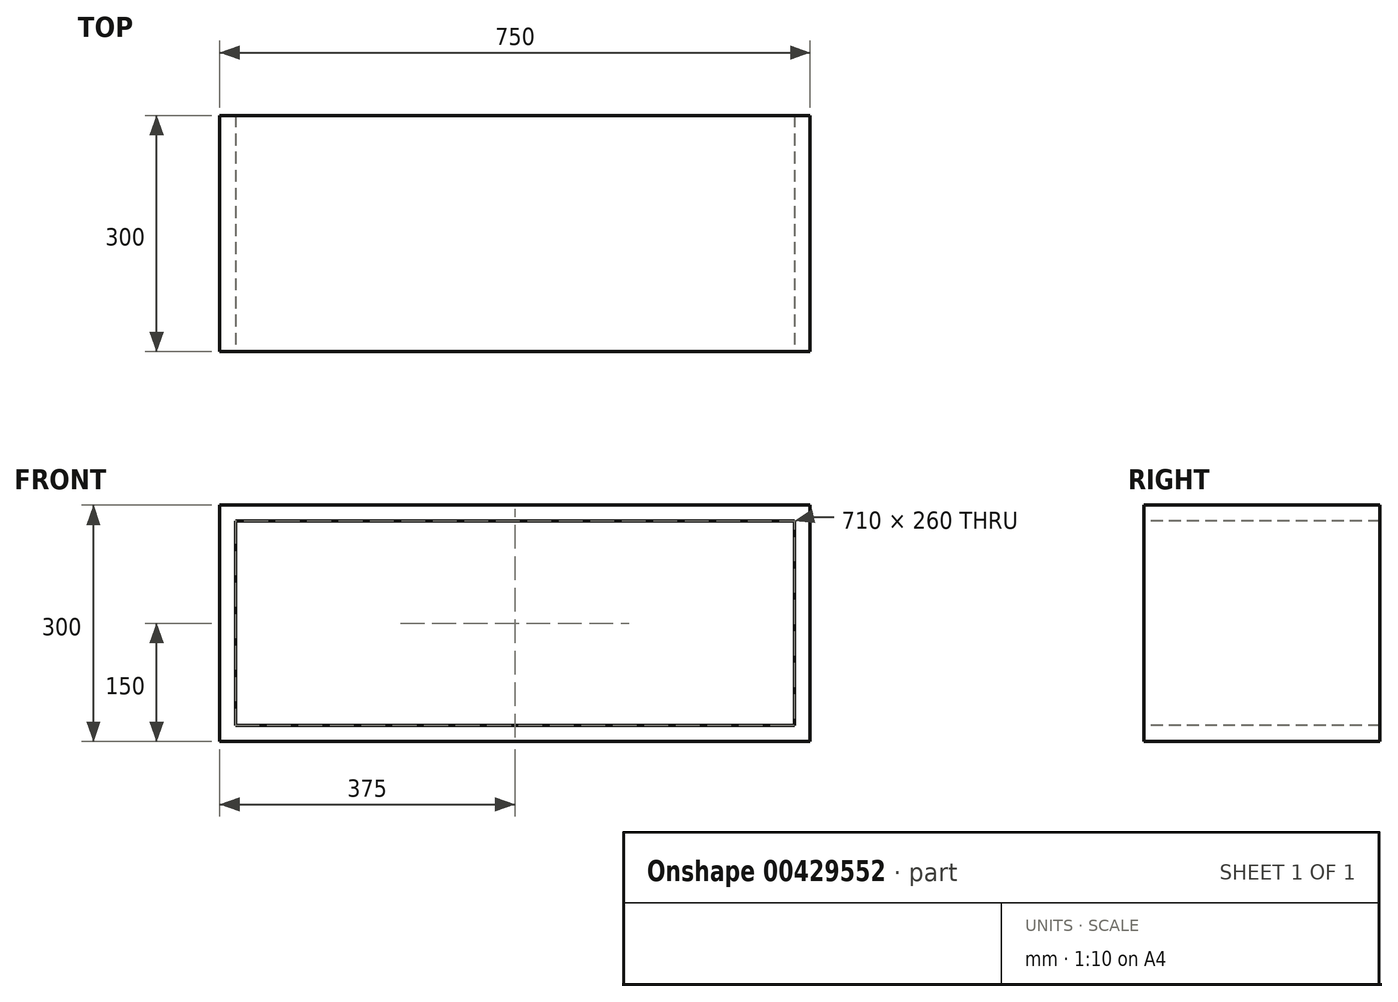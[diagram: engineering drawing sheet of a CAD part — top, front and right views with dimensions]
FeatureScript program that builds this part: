
annotation { "Feature Type Name" : "Feature", "Feature Type Description" : "" }
export const myFeature = defineFeature(function(context is Context, id is Id, definition is map)
    precondition{}
    {
        {
            var Q0;
            Q0=qCreatedBy(makeId("Front.planeOp"),FACE);
            var sketch = newSketch(context, id + "F0", { "sketchPlane" : qUnion([Q0])});
            skLineSegment(sketch, "E0.bottom", {"start": v(375, -150) * mm, "end": v(-375, -150) * mm});
            skLineSegment(sketch, "E0.top", {"start": v(375, 150) * mm, "end": v(-375, 150) * mm});
            skLineSegment(sketch, "E0.left", {"start": v(375, -150) * mm, "end": v(375, 150) * mm});
            skLineSegment(sketch, "E0.right", {"start": v(-375, -150) * mm, "end": v(-375, 150) * mm});
            skPoint(sketch, "E0.middle", {"position": v(0, 0) * mm});
            skLineSegment(sketch, "E1.0", {"start": v(355, -150) * mm, "end": v(355, 150) * mm});
            skLineSegment(sketch, "E2.0", {"start": v(375, 130) * mm, "end": v(-375, 130) * mm});
            skLineSegment(sketch, "E3.0", {"start": v(-355, -150) * mm, "end": v(-355, 150) * mm});
            skLineSegment(sketch, "E4.0", {"start": v(375, -130) * mm, "end": v(-375, -130) * mm});
            skSolve(sketch);
        }
        {
            var Q0;
            {var subQ0=sQuery(id+"F0.wireOp",EDGE,"E1.0");var subQ1=sQuery(id+"F0.wireOp",EDGE,"E0.top");var subQ2=makeQuery(id+"F0.imprint","INTERSECT",VERTEX,{"derivedFrom":[subQ1,subQ0]});Q0=makeQuery(id+"F0.imprint","IMPRINT",FACE,{"disambiguationData":[TD([[makeQuery(id+"F0.imprint","IMPRINT",EDGE,{"disambiguationData":[TD([[subQ2,-1.0]])],"derivedFrom":subQ1}),1.0]])]});}
            var Q1;
            {var subQ0=sQuery(id+"F0.wireOp",EDGE,"E0.right");var subQ1=sQuery(id+"F0.wireOp",EDGE,"E0.top");var subQ2=makeQuery(id+"F0.imprint","INTERSECT",VERTEX,{"derivedFrom":[subQ1,subQ0]});Q1=makeQuery(id+"F0.imprint","IMPRINT",FACE,{"disambiguationData":[TD([[makeQuery(id+"F0.imprint","IMPRINT",EDGE,{"disambiguationData":[TD([[subQ2,1.0]])],"derivedFrom":subQ1}),1.0]])]});}
            var Q2;
            {var subQ0=sQuery(id+"F0.wireOp",EDGE,"E2.0");var subQ1=sQuery(id+"F0.wireOp",EDGE,"E0.right");var subQ2=makeQuery(id+"F0.imprint","INTERSECT",VERTEX,{"derivedFrom":[subQ1,subQ0]});Q2=makeQuery(id+"F0.imprint","IMPRINT",FACE,{"disambiguationData":[TD([[makeQuery(id+"F0.imprint","IMPRINT",EDGE,{"disambiguationData":[TD([[subQ2,1.0]])],"derivedFrom":subQ1}),-1.0]])]});}
            var Q3;
            {var subQ0=sQuery(id+"F0.wireOp",EDGE,"E0.right");var subQ1=sQuery(id+"F0.wireOp",EDGE,"E0.bottom");var subQ2=makeQuery(id+"F0.imprint","INTERSECT",VERTEX,{"derivedFrom":[subQ1,subQ0]});Q3=makeQuery(id+"F0.imprint","IMPRINT",FACE,{"disambiguationData":[TD([[makeQuery(id+"F0.imprint","IMPRINT",EDGE,{"disambiguationData":[TD([[subQ2,1.0]])],"derivedFrom":subQ1}),-1.0]])]});}
            var Q4;
            {var subQ0=sQuery(id+"F0.wireOp",EDGE,"E1.0");var subQ1=sQuery(id+"F0.wireOp",EDGE,"E0.bottom");var subQ2=makeQuery(id+"F0.imprint","INTERSECT",VERTEX,{"derivedFrom":[subQ1,subQ0]});Q4=makeQuery(id+"F0.imprint","IMPRINT",FACE,{"disambiguationData":[TD([[makeQuery(id+"F0.imprint","IMPRINT",EDGE,{"disambiguationData":[TD([[subQ2,-1.0]])],"derivedFrom":subQ1}),-1.0]])]});}
            var Q5;
            {var subQ0=sQuery(id+"F0.wireOp",EDGE,"E0.left");var subQ1=sQuery(id+"F0.wireOp",EDGE,"E0.bottom");var subQ2=makeQuery(id+"F0.imprint","INTERSECT",VERTEX,{"derivedFrom":[subQ1,subQ0]});Q5=makeQuery(id+"F0.imprint","IMPRINT",FACE,{"disambiguationData":[TD([[makeQuery(id+"F0.imprint","IMPRINT",EDGE,{"disambiguationData":[TD([[subQ2,-1.0]])],"derivedFrom":subQ1}),-1.0]])]});}
            var Q6;
            {var subQ0=sQuery(id+"F0.wireOp",EDGE,"E2.0");var subQ1=sQuery(id+"F0.wireOp",EDGE,"E0.left");var subQ2=makeQuery(id+"F0.imprint","INTERSECT",VERTEX,{"derivedFrom":[subQ1,subQ0]});Q6=makeQuery(id+"F0.imprint","IMPRINT",FACE,{"disambiguationData":[TD([[makeQuery(id+"F0.imprint","IMPRINT",EDGE,{"disambiguationData":[TD([[subQ2,1.0]])],"derivedFrom":subQ1}),1.0]])]});}
            var Q7;
            {var subQ0=sQuery(id+"F0.wireOp",EDGE,"E0.left");var subQ1=sQuery(id+"F0.wireOp",EDGE,"E0.top");var subQ2=makeQuery(id+"F0.imprint","INTERSECT",VERTEX,{"derivedFrom":[subQ1,subQ0]});Q7=makeQuery(id+"F0.imprint","IMPRINT",FACE,{"disambiguationData":[TD([[makeQuery(id+"F0.imprint","IMPRINT",EDGE,{"disambiguationData":[TD([[subQ2,-1.0]])],"derivedFrom":subQ1}),1.0]])]});}
            extrude(context, id + "F1", {"entities" : qUnion([Q0, Q1, Q2, Q3, Q4, Q5, Q6, Q7]), "oppositeDirection" : true, "depth" : 300 * mm});
        }
    });
